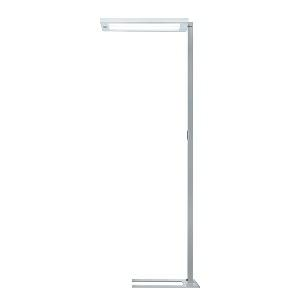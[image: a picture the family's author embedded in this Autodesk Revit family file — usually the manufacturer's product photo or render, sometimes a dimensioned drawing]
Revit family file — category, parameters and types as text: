
# Revit family: lavigo_-_dps_14000_840_d_g2_00803270_9630
name_source: partatom
category: Lighting Fixtures
units: mm (PartAtom-declared; Revit-internal decimal feet)

## family parameters
Cut with Voids When Loaded = No
Host = Face
Light Source = No
Part Type = Normal
Room Calculation Point = No
Round Connector Dimension = Use Diameter
Shared = No

## types (1)
- LAVIGO - DPS 14000/840/D/G2 (1 x LED, 14050 lm, 4000K)
    Apparent Load = 93 VA
    Approval mark = CE
    CIE Flux Codes = 60 87 97 12 100
    Color Rendering = 80-89
    Color Temperature = 4000K
    Control Gear = Electronic ballast
    Default Elevation = 1800 mm
    Description = DPS 14000/840/D/G2|Free-standing luminaire|light source: LED|work equipment: Electronic ballast|connected load: 220-240 V, 50/60 Hz|Power consumption: approx. 93 W|standby: approx. 0,50|power factor: approx. 0,943|luminous flux: 14050 lm|luminous efficacy: 151 lm/W|light distribution: Direct/indirect|direct ratio: approx. 13 %|colour temperature: Cold white, ca. 4000 K|color rendering index (CRI): >= 80|chromaticity tolerance:  3 SDCM|technology: Continuously dimmable|operation: Multi-function switch|luminaire body|material: Steel/plastic|surface: Painted|colour: Silver metallic|lamp cover: Acrylic (PMMA), Satine|tubular section|material: Steel tube|surface: Painted|Form: Tubular section upright|colour of tubular section: Silver metallic|luminaire base|Form: C-form flat|weight (net): approx. 19.7 kg|mains lead: 3.00 m Mains plug CEE 7/VII|Fastening: Floor standing base|decorative contrast side parts: Flint grey|glare control: Prism aperture|luminance(L65): <= 3000 cd/m|unified glare rating(4H 8H): <=  16|special features: Luminaire head detachable, Cradle to Cradle Certified TM, Direct light component with edge light and light-guide technology for homogenous light exit, Flicker-free, Separated, direct and indirect light individually adjustable|Approval mark: VDE - ENEC|
    Frequency = 50 Hz
    Height = 36 mm
    Lamp = 1 x LED
    Lamp Light Flux = 14050 lm
    Lamp count = 1
    Length = 675 mm
    Luminous efficacy = 151 lm/W
    Manufacturer = Waldmann
    ModVariant = No
    Model = 00803270
    Mounting Place = Floor
    Mounting Type = Freestanding
    Number of Poles = 1
    OnlyDefault = Yes
    Power Factor = 1
    Product Name = LAVIGO - DPS 14000/840/D/G2
    Product group = Free standing luminaire
    ProductGroupID = 13
    Protection Class = Protection class I
    Protection Degree = IP 20
    RLX_Detail_Level = 1
    RLX_Emergency_Light_Flux = 0 lm
    RLX_Emergency_Type = 0
    RLX_Emergency_Type_DB = No
    RlxData = <blob elided: 36865 chars, md5=181a624d>
    Socket = socket
    Standby Power = 0 W
    System Light Flux = 14050 lm
    System Power = 93 W
    Type Comments = Product without accessories
    Type Image = 121695000-00625713.jpg
    URL = http://relux.com
    VarID = ---
    Voltage = 230 V
    Voltage Range = 220-240 V
    Weight = 0.00 kg
    Width = 320 mm

## geometry (parser evidence)
native form markers: Blend x4, Sweep x15
no freeform markers — native parametric forms only
